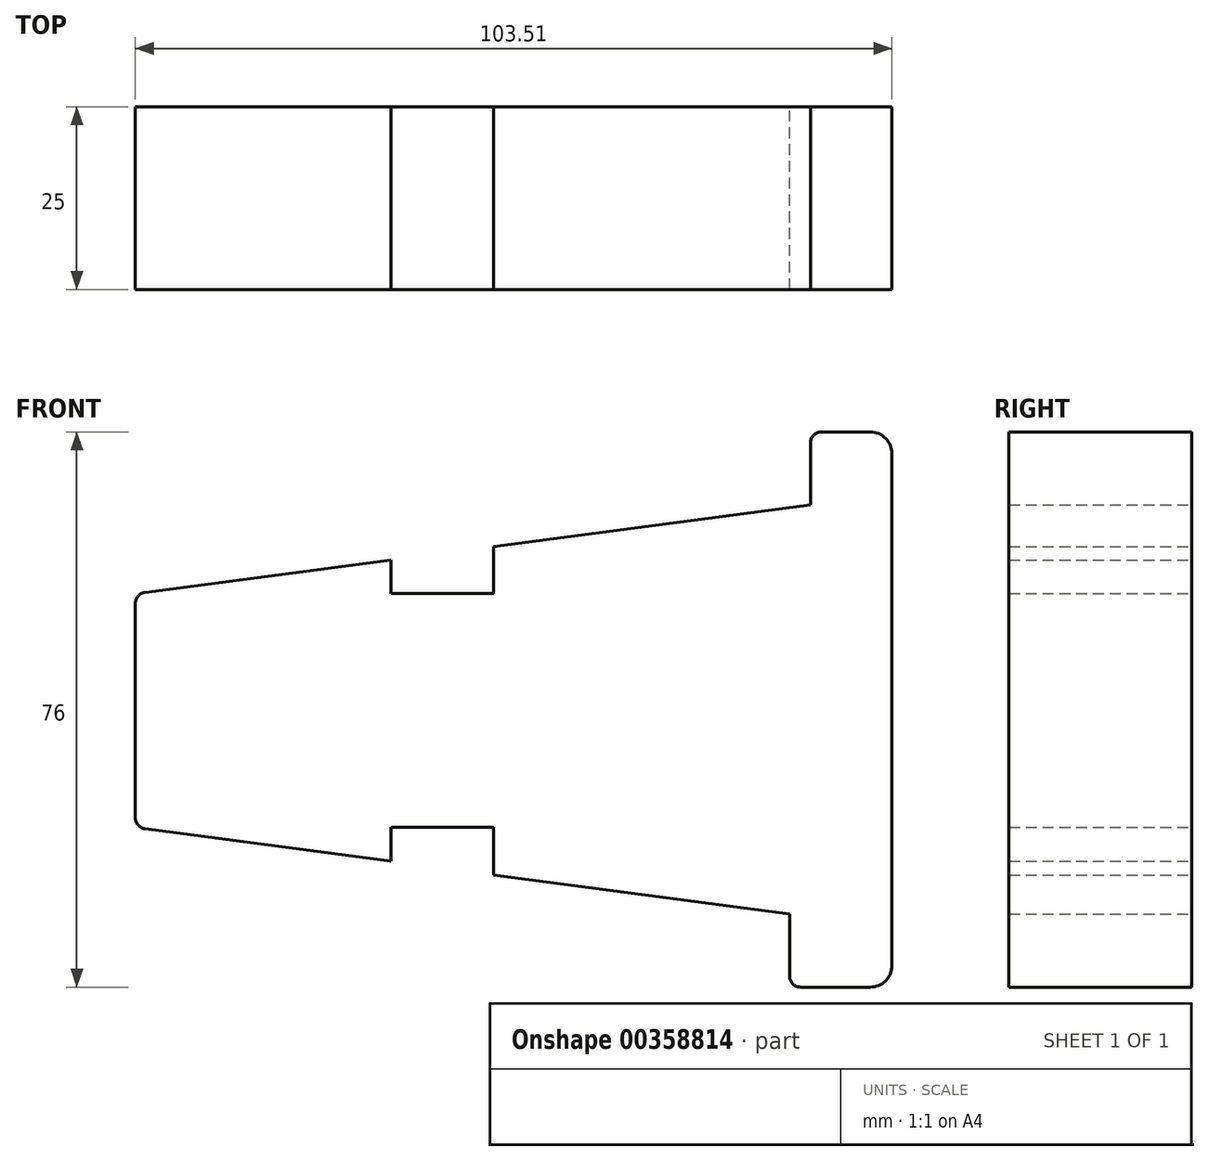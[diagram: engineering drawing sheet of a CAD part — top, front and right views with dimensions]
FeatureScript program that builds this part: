
annotation { "Feature Type Name" : "Feature", "Feature Type Description" : "" }
export const myFeature = defineFeature(function(context is Context, id is Id, definition is map)
    precondition{}
    {
        {
            var Q0;
            Q0=qCreatedBy(makeId("Front.planeOp"),FACE);
            var sketch = newSketch(context, id + "F0", { "sketchPlane" : qUnion([Q0])});
            skLineSegment(sketch, "E0", {"start": v(25.48, 9.24) * mm, "end": v(18.82, 9.24) * mm});
            skLineSegment(sketch, "E1", {"start": v(17.32, 7.74) * mm, "end": v(17.32, -0.76) * mm});
            skLineSegment(sketch, "E2", {"start": v(-73.42, -12.69) * mm, "end": v(-40.03, -8.3) * mm});
            skPoint(sketch, "E3", {"position": v(-40.03, -8.3) * mm});
            skLineSegment(sketch, "E4", {"start": v(-40.03, -8.3) * mm, "end": v(-40.03, -12.9) * mm});
            skLineSegment(sketch, "E5", {"start": v(-40.03, -12.9) * mm, "end": v(-26.03, -12.9) * mm});
            skLineSegment(sketch, "E6", {"start": v(-26.03, -6.46) * mm, "end": v(17.32, -0.76) * mm});
            skLineSegment(sketch, "E7", {"start": v(-26.03, -12.9) * mm, "end": v(-26.03, -6.46) * mm});
            skPoint(sketch, "E8.visualSharp", {"position": v(-75.03, -44.9) * mm});
            skPoint(sketch, "E9.visualSharp", {"position": v(-75.03, -12.9) * mm});
            skPoint(sketch, "E10.visualSharp", {"position": v(28.62, -44.88) * mm});
            skPoint(sketch, "E11.visualSharp", {"position": v(17.32, 9.24) * mm});
            skArc(sketch, "E11.filletArc", {"start": v(18.82, 9.24) * mm, "mid": v(17.76, 8.8) * mm, "end": v(17.32, 7.74) * mm});
            skPoint(sketch, "E12.visualSharp", {"position": v(28.78, 9.24) * mm});
            skArc(sketch, "E12.filletArc", {"start": v(28.48, 6.24) * mm, "mid": v(27.6, 8.36) * mm, "end": v(25.48, 9.24) * mm});
            skLineSegment(sketch, "E13", {"start": v(28.48, 6.24) * mm, "end": v(28.48, -63.76) * mm});
            skLineSegment(sketch, "E14", {"start": v(25.48, -66.76) * mm, "end": v(15.98, -66.76) * mm});
            skLineSegment(sketch, "E15", {"start": v(14.48, -65.26) * mm, "end": v(14.48, -56.76) * mm});
            skPoint(sketch, "E16.visualSharp", {"position": v(28.48, -66.76) * mm});
            skArc(sketch, "E16.filletArc", {"start": v(25.48, -66.76) * mm, "mid": v(27.6, -65.88) * mm, "end": v(28.48, -63.76) * mm});
            skPoint(sketch, "E17.visualSharp", {"position": v(14.48, -66.76) * mm});
            skArc(sketch, "E17.filletArc", {"start": v(14.48, -65.26) * mm, "mid": v(14.92, -66.32) * mm, "end": v(15.98, -66.76) * mm});
            skLineSegment(sketch, "E18", {"start": v(-73.42, -12.69) * mm, "end": v(-73.73, -12.73) * mm});
            skLineSegment(sketch, "E19", {"start": v(-75.03, -14.22) * mm, "end": v(-75.03, -43.59) * mm});
            skLineSegment(sketch, "E20", {"start": v(-73.73, -45.07) * mm, "end": v(-40.03, -49.54) * mm});
            skLineSegment(sketch, "E21", {"start": v(-40.03, -44.9) * mm, "end": v(-26.03, -44.9) * mm});
            skLineSegment(sketch, "E22", {"start": v(-26.03, -44.9) * mm, "end": v(-26.03, -51.4) * mm});
            skLineSegment(sketch, "E23", {"start": v(-40.03, -44.9) * mm, "end": v(-40.03, -49.54) * mm});
            skLineSegment(sketch, "E24.trimOffspring", {"start": v(-26.03, -51.4) * mm, "end": v(14.48, -56.76) * mm});
            skArc(sketch, "E25.filletArc", {"start": v(-73.73, -12.73) * mm, "mid": v(-74.66, -13.23) * mm, "end": v(-75.03, -14.22) * mm});
            skArc(sketch, "E26.filletArc", {"start": v(-75.03, -43.59) * mm, "mid": v(-74.66, -44.57) * mm, "end": v(-73.73, -45.07) * mm});
            skSolve(sketch);
        }
        {
            var Q0;
            Q0 = qSketchRegion(id + "F0", true);
            extrude(context, id + "F1", {"entities" : qUnion([Q0]), "depth" : 25 * mm});
        }
    });
